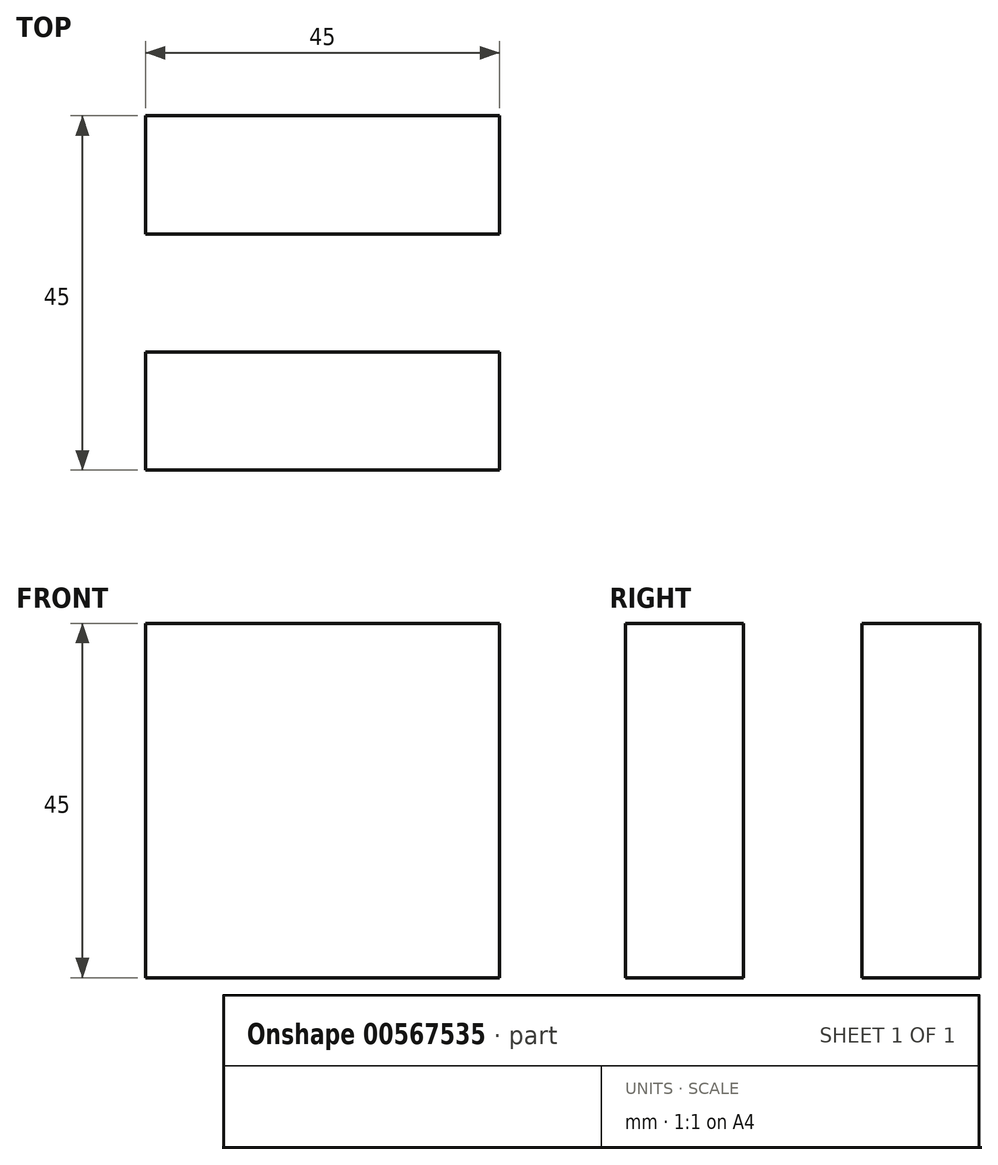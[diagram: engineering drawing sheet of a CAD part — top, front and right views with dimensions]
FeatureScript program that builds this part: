
annotation { "Feature Type Name" : "Feature", "Feature Type Description" : "" }
export const myFeature = defineFeature(function(context is Context, id is Id, definition is map)
    precondition{}
    {
        {
            var Q0;
            Q0=qCreatedBy(makeId("Top.planeOp"),FACE);
            var sketch = newSketch(context, id + "F0", { "sketchPlane" : qUnion([Q0])});
            skLineSegment(sketch, "E0.bottom", {"start": v(-500, -22.5) * mm, "end": v(500, -22.5) * mm});
            skLineSegment(sketch, "E0.top", {"start": v(-500, 22.5) * mm, "end": v(500, 22.5) * mm});
            skLineSegment(sketch, "E0.left", {"start": v(-500, -22.5) * mm, "end": v(-500, 22.5) * mm});
            skLineSegment(sketch, "E0.right", {"start": v(500, -22.5) * mm, "end": v(500, 22.5) * mm});
            skPoint(sketch, "E0.middle", {"position": v(0, 0) * mm});
            skLineSegment(sketch, "E1", {"start": v(500, -22.5) * mm, "end": v(500, -7.5) * mm});
            skLineSegment(sketch, "E2", {"start": v(500, 22.5) * mm, "end": v(500, 7.5) * mm});
            skLineSegment(sketch, "E3", {"start": v(500, -7.5) * mm, "end": v(455, -7.5) * mm});
            skLineSegment(sketch, "E4", {"start": v(500, 7.5) * mm, "end": v(455, 7.5) * mm});
            skLineSegment(sketch, "E5", {"start": v(455, -7.5) * mm, "end": v(455, -22.5) * mm});
            skLineSegment(sketch, "E6", {"start": v(455, 7.5) * mm, "end": v(455, 22.5) * mm});
            skLineSegment(sketch, "E7", {"start": v(-500, 22.5) * mm, "end": v(-500, 7.5) * mm});
            skLineSegment(sketch, "E8", {"start": v(-500, -22.5) * mm, "end": v(-500, -7.5) * mm});
            skLineSegment(sketch, "E9", {"start": v(-500, 7.5) * mm, "end": v(-455, 7.5) * mm});
            skLineSegment(sketch, "E10", {"start": v(-500, -7.5) * mm, "end": v(-455, -7.5) * mm});
            skLineSegment(sketch, "E11", {"start": v(-455, -7.5) * mm, "end": v(-455, -22.5) * mm});
            skLineSegment(sketch, "E12", {"start": v(-455, 7.5) * mm, "end": v(-455, 22.5) * mm});
            skSolve(sketch);
        }
        {
            var Q0;
            Q0=makeQuery(id+"F0.imprint","IMPRINT",FACE,{"disambiguationData":[TD([[makeQuery(id+"F0.imprint","IMPRINT",EDGE,{"derivedFrom":sQuery(id+"F0.wireOp",EDGE,"E0.left")}),-1.0]])]});
            extrude(context, id + "F1", {"entities" : qUnion([Q0]), "depth" : 45 * mm, "offsetDistance" : 25 * mm});
        }
    });
